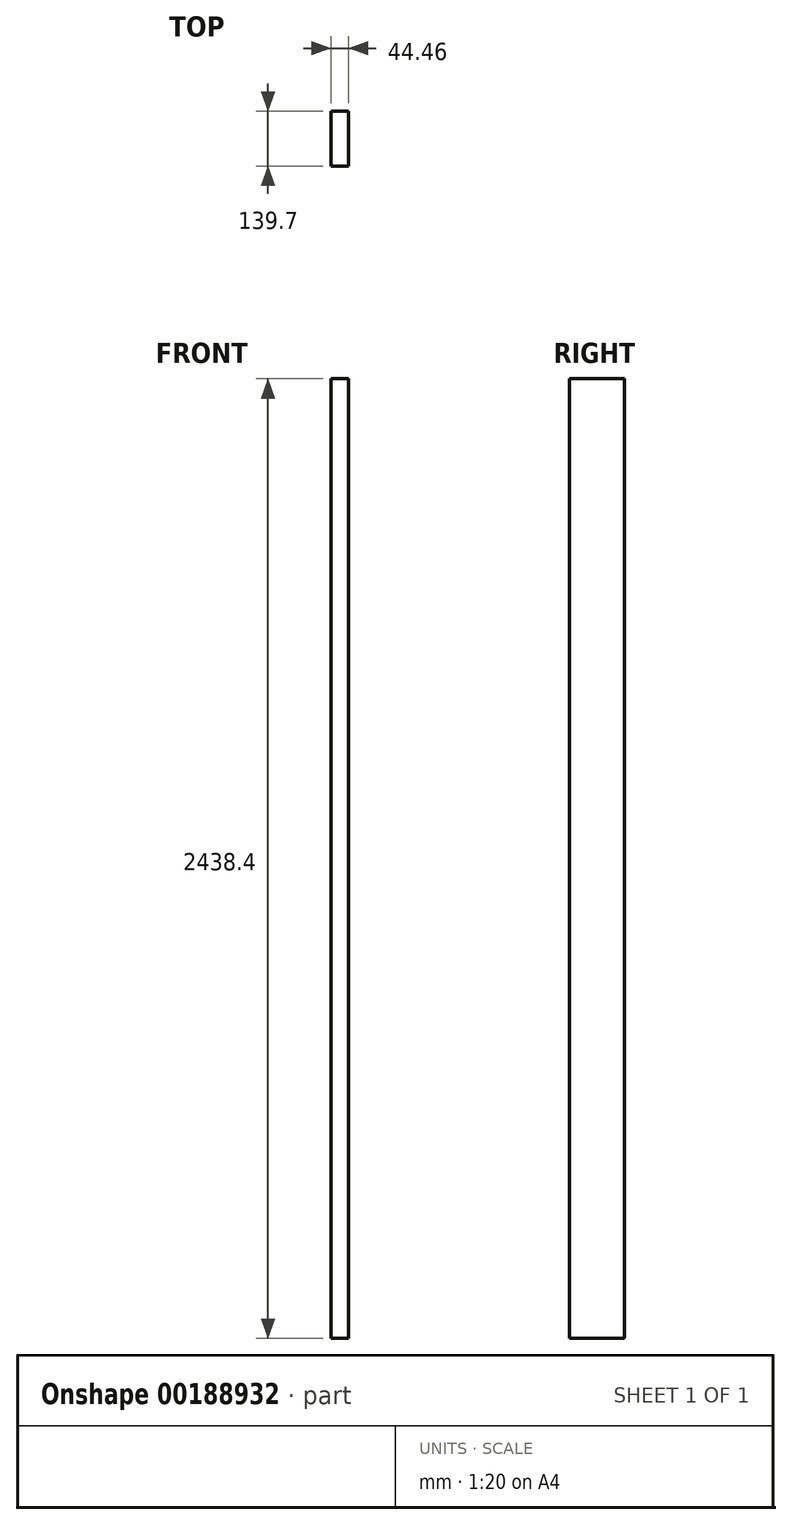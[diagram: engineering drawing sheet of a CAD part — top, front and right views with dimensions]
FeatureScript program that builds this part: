
annotation { "Feature Type Name" : "Feature", "Feature Type Description" : "" }
export const myFeature = defineFeature(function(context is Context, id is Id, definition is map)
    precondition{}
    {
        {
            var Q0;
            Q0=qCreatedBy(makeId("Top.planeOp"),FACE);
            var sketch = newSketch(context, id + "F1", { "sketchPlane" : qUnion([Q0])});
            skLineSegment(sketch, "E0.bottom", {"start": v(22.23, -69.85) * mm, "end": v(-22.22, -69.85) * mm});
            skLineSegment(sketch, "E0.top", {"start": v(22.22, 69.85) * mm, "end": v(-22.23, 69.85) * mm});
            skLineSegment(sketch, "E0.left", {"start": v(22.23, -69.85) * mm, "end": v(22.22, 69.85) * mm});
            skLineSegment(sketch, "E0.right", {"start": v(-22.22, -69.85) * mm, "end": v(-22.23, 69.85) * mm});
            skPoint(sketch, "E0.middle", {"position": v(0, 0) * mm});
            skSolve(sketch);
        }
        {
            var Q0;
            Q0=makeQuery(id+"F1.imprint","IMPRINT",FACE,{"disambiguationData":[TD([[makeQuery(id+"F1.imprint","IMPRINT",EDGE,{"derivedFrom":sQuery(id+"F1.wireOp",EDGE,"E0.bottom")}),-1.0]])]});
            extrude(context, id + "F0", {"entities" : qUnion([Q0]), "endBound" : BoundingType.SYMMETRIC, "depth" : 2438.4 * mm});
        }
    });
